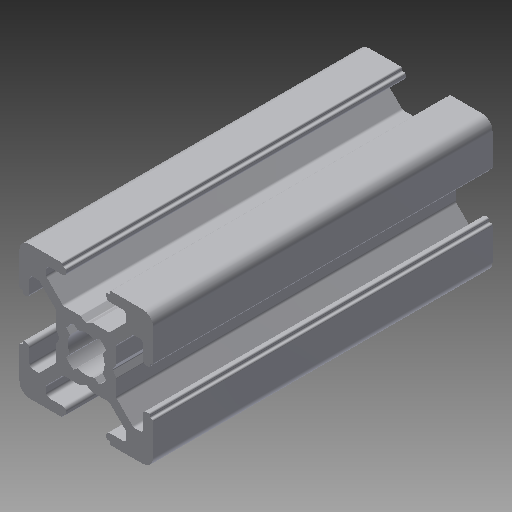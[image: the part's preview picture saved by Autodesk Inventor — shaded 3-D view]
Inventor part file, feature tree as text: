
AUTODESK INVENTOR PART (.ipt)
format: ipt  version: 2019 (Build 230136000, 136)  size: 339,456 bytes
history: native  units: in
note: dims shown in document units (in); Inventor stores cm internally (conversion verified against a paired STEP export)
features: other x3, extrude x1, sketch x1
ambient origin geometry x8: Origin, YZ Plane, XZ Plane, XY Plane, X Axis, Y Axis, Z Axis, Center Point
bodies: Solid1 (feature_tree)
feature tree (5):
  other  "Blocks"
  extrude  "Extrusion1"  Depth=1.0in
  sketch  "Sketch1"  dims[d1=0.0in d13=1.0in d14=1.0in]
  other  "20x20"
  other  "20x20:1"
